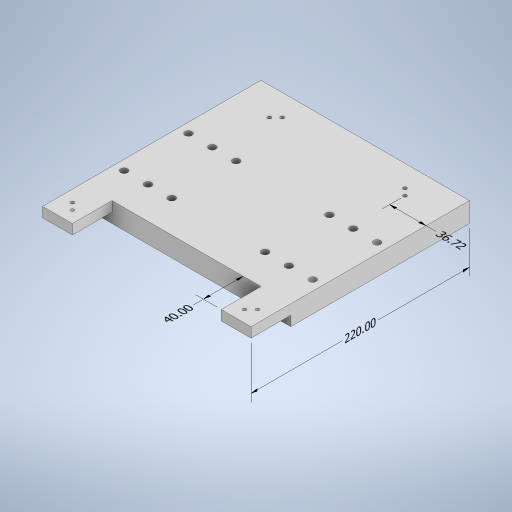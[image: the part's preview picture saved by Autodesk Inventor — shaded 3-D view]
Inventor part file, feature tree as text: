
AUTODESK INVENTOR PART (.ipt)
format: ipt  version: 2023 (Build 270158000, 158)  size: 327,168 bytes
history: native  units: mm
features: other x5, sketch x5, extrude x4, hole x1
ambient origin geometry x8: Origin, YZ Plane, XZ Plane, XY Plane, X Axis, Y Axis, Z Axis, Center Point
bodies: Body1 (feature_tree)
feature tree (15):
  other  "Sólido1"
  other  "Anotaciones"
  extrude  "Extrusión1"  Depth=180.0mm
  extrude  "Extrusión2"  Depth=10.0mm
  extrude  "Extrusión7"  Depth=20.0mm TaperAngle=0.0deg
  hole  "Agujero1"  [1 undecoded]
  extrude  "Extrusión8"  Depth=20.0mm TaperAngle=0.0deg
  sketch  "Boceto1"  dims[d0=210.0mm d1=180.0mm]
  sketch  "Boceto2"  dims[d2=20.0mm d3=0.0mm]
  sketch  "Boceto7"  dims[d4=7.0mm d5=68.0mm d6=80.0mm d7=7.6mm d8=10.0mm d9=7.0mm d11=24.0mm d14=10.0mm d16=10.0mm]
  sketch  "Boceto8"  dims[d28=20.0mm d29=0.0mm d30=20.0mm d31=0.0mm]
  sketch  "Boceto9"  dims[d32=15.0mm d55=40.0mm d56=0.0mm d67=11.749873mm d70=3.5mm d71=6.0mm d72=4.0mm d73=2.0mm d74=90.0deg d75=8.0mm d76=20.594885mm d77=20.0mm d78=0.0mm d79=29.999873mm d80=10.0mm d81=0.0mm d82=10.0mm d83=29.999873mm d84=0.0mm d86=40.0mm d87=29.999873mm d88=21.75mm d89=11.75mm d90=28.300341mm d91=11.749873mm d101=25.0mm d102=40.0mm d100=40.0mm d93=5.753731mm d94=3.436935mm d95=220.0mm d96=1.496228mm d97=36.721397mm d98=7.257763mm d99=9.275157mm]
  other  "Cota lineal 1"
  other  "Cota lineal 2"
  other  "Cota lineal 3"
note: 1 required parameter value undecoded (feature->parameter linkage not recoverable at this tier; creation-order binding heuristic only, values carry confidence <= 0.55)
